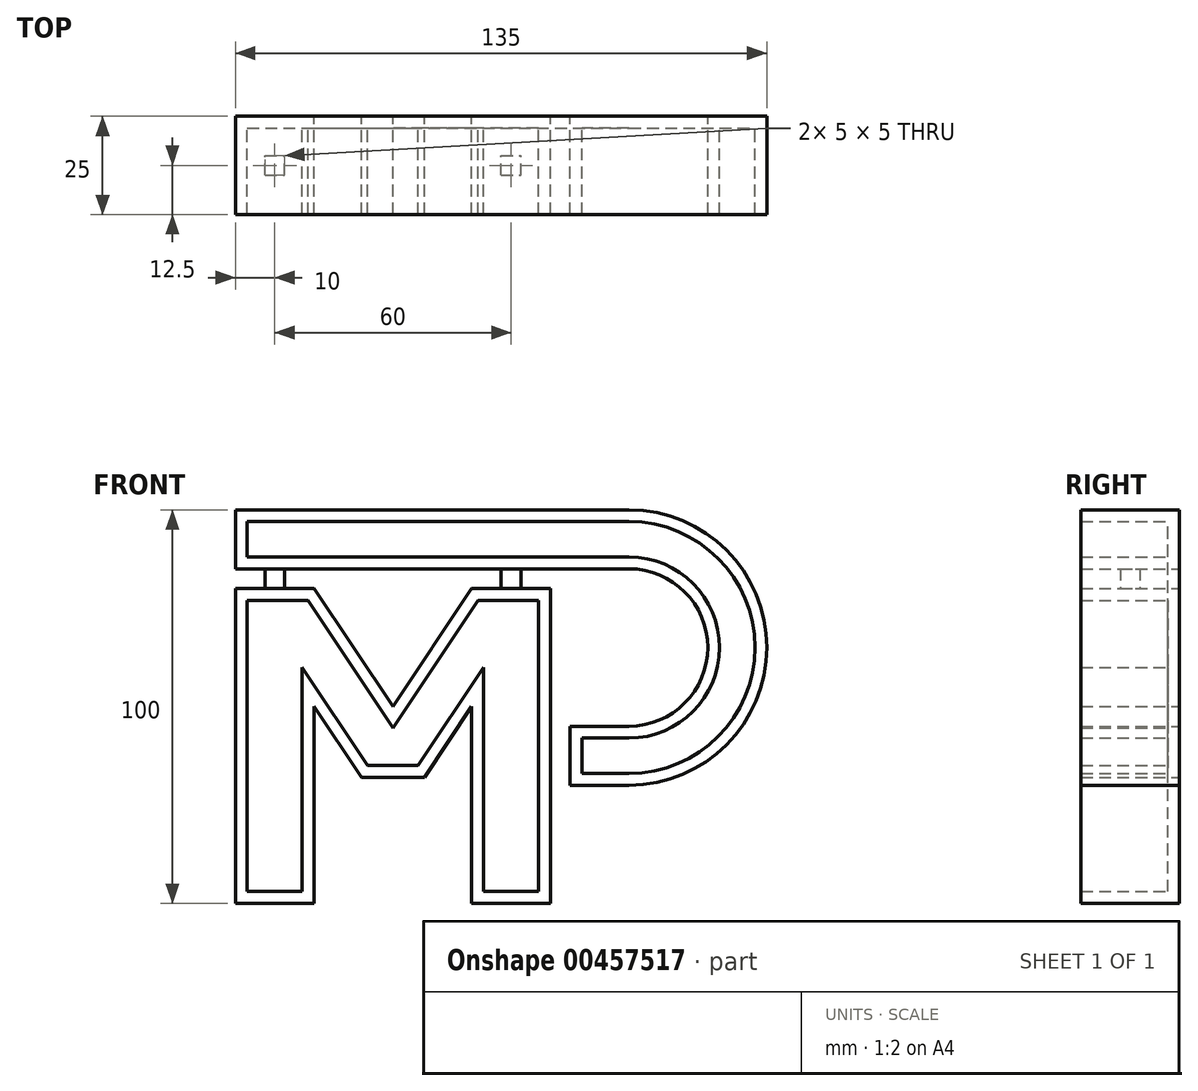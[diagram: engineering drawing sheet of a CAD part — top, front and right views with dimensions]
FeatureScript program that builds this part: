
annotation { "Feature Type Name" : "Feature", "Feature Type Description" : "" }
export const myFeature = defineFeature(function(context is Context, id is Id, definition is map)
    precondition{}
    {
        {
            var Q0;
            Q0=qCreatedBy(makeId("Top.planeOp"),FACE);
            cPlane(context, id + "F0", {"entities" : qUnion([Q0]), "cplaneType" : CPlaneType.OFFSET, "offset" : 80 * mm, "width" : 150 * mm, "height" : 150 * mm});
        }
        {
            var Q0;
            Q0=qCreatedBy(makeId("Front.planeOp"),FACE);
            var sketch = newSketch(context, id + "F1", { "sketchPlane" : qUnion([Q0])});
            skLineSegment(sketch, "E0", {"start": v(-40, 0) * mm, "end": v(-40, 80) * mm});
            skLineSegment(sketch, "E1", {"start": v(-40, 80) * mm, "end": v(-20, 80) * mm});
            skLineSegment(sketch, "E2", {"start": v(-20, 80) * mm, "end": v(0, 50) * mm});
            skLineSegment(sketch, "E3", {"start": v(-20, 0) * mm, "end": v(-20, 50) * mm});
            skLineSegment(sketch, "E4", {"start": v(0, 30) * mm, "end": v(0, 30) * mm});
            skLineSegment(sketch, "E5", {"start": v(-20, 50) * mm, "end": v(-8, 32) * mm});
            skLineSegment(sketch, "E6", {"start": v(-8, 32) * mm, "end": v(0, 32) * mm});
            skLineSegment(sketch, "E7.MirrorCS", {"start": v(20, 80) * mm, "end": v(0, 50) * mm});
            skLineSegment(sketch, "E8.MirrorCS", {"start": v(40, 80) * mm, "end": v(20, 80) * mm});
            skLineSegment(sketch, "E9.MirrorCS", {"start": v(40, 0) * mm, "end": v(40, 80) * mm});
            skLineSegment(sketch, "E10.MirrorCS", {"start": v(40, 0) * mm, "end": v(20, 0) * mm});
            skLineSegment(sketch, "E11.MirrorCS", {"start": v(20, 0) * mm, "end": v(20, 50) * mm});
            skLineSegment(sketch, "E12.MirrorCS", {"start": v(20, 50) * mm, "end": v(8, 32) * mm});
            skLineSegment(sketch, "E13.MirrorCS", {"start": v(8, 32) * mm, "end": v(0, 32) * mm});
            skLineSegment(sketch, "E14", {"start": v(-40, 0) * mm, "end": v(-20, 0) * mm});
            skSolve(sketch);
        }
        {
            var Q0;
            Q0=qCreatedBy(makeId("Front.planeOp"),FACE);
            var sketch = newSketch(context, id + "F2", { "sketchPlane" : qUnion([Q0])});
            skLineSegment(sketch, "E15", {"start": v(-40, 85) * mm, "end": v(60, 85) * mm});
            skLineSegment(sketch, "E16", {"start": v(-40, 85) * mm, "end": v(-40, 100) * mm});
            skLineSegment(sketch, "E17", {"start": v(-40, 100) * mm, "end": v(60, 100) * mm});
            skLineSegment(sketch, "E18", {"start": v(60, 45) * mm, "end": v(45, 45) * mm});
            skLineSegment(sketch, "E19", {"start": v(45, 45) * mm, "end": v(45, 30) * mm});
            skLineSegment(sketch, "E20", {"start": v(45, 30) * mm, "end": v(60, 30) * mm});
            skArc(sketch, "E21", {"start": v(60, 85) * mm, "mid": v(80, 65) * mm, "end": v(60, 45) * mm});
            skArc(sketch, "E22", {"start": v(60, 100) * mm, "mid": v(95, 65) * mm, "end": v(60, 30) * mm});
            skSolve(sketch);
        }
        {
            var Q0;
            Q0 = qSketchRegion(id + "F1", true);
            var Q1;
            Q1 = qSketchRegion(id + "F2", true);
            var Q2;
            Q2=makeQuery(id+"F2.imprint","IMPRINT",FACE,{"disambiguationData":[TD([[makeQuery(id+"F2.imprint","IMPRINT",EDGE,{"derivedFrom":sQuery(id+"F2.wireOp",EDGE,"E15")}),1.0]])]});
            var Q3;
            Q3=makeQuery(id+"F1.imprint","IMPRINT",FACE,{"disambiguationData":[TD([[makeQuery(id+"F1.imprint","IMPRINT",EDGE,{"derivedFrom":sQuery(id+"F1.wireOp",EDGE,"E0")}),-1.0]])]});
            extrude(context, id + "F3", {"entities" : qUnion([Q0, Q1, Q2, Q3]), "depth" : 25 * mm});
        }
        {
            var Q0;
            Q0=makeQuery(id+"F3.opExtrude","CAP_FACE",FACE,{"disambiguationData":[OSD([sQuery(id+"F1.wireOp",EDGE,"E0"),sQuery(id+"F1.wireOp",EDGE,"E1"),sQuery(id+"F1.wireOp",EDGE,"E2"),sQuery(id+"F1.wireOp",EDGE,"ab83c112-5276-4321-8634-02bc0d65a358"),sQuery(id+"F1.wireOp",EDGE,"E3"),sQuery(id+"F1.wireOp",EDGE,"E5"),sQuery(id+"F1.wireOp",EDGE,"E6"),sQuery(id+"F1.wireOp",EDGE,"E7.MirrorCS"),sQuery(id+"F1.wireOp",EDGE,"E8.MirrorCS"),sQuery(id+"F1.wireOp",EDGE,"E9.MirrorCS"),sQuery(id+"F1.wireOp",EDGE,"E10.MirrorCS"),sQuery(id+"F1.wireOp",EDGE,"E11.MirrorCS"),sQuery(id+"F1.wireOp",EDGE,"E12.MirrorCS"),sQuery(id+"F1.wireOp",EDGE,"E13.MirrorCS")])],"isStart":false});
            var Q1;
            Q1=makeQuery(id+"F3.opExtrude","CAP_FACE",FACE,{"disambiguationData":[OSD([sQuery(id+"F2.wireOp",EDGE,"E15"),sQuery(id+"F2.wireOp",EDGE,"E16"),sQuery(id+"F2.wireOp",EDGE,"E17"),sQuery(id+"F2.wireOp",EDGE,"E18"),sQuery(id+"F2.wireOp",EDGE,"E19"),sQuery(id+"F2.wireOp",EDGE,"E20"),sQuery(id+"F2.wireOp",EDGE,"E21"),sQuery(id+"F2.wireOp",EDGE,"E22")])],"isStart":false});
            shell(context, id + "F4", {"entities" : qUnion([Q0, Q1]), "thickness" : 3 * mm});
        }
        {
            var Q0;
            Q0=qCreatedBy(id+"F0.planeOp",FACE);
            var sketch = newSketch(context, id + "F5", { "sketchPlane" : qUnion([Q0])});
            skLineSegment(sketch, "E23.bottom", {"start": v(-32.5, -15) * mm, "end": v(-27.5, -15) * mm});
            skLineSegment(sketch, "E23.top", {"start": v(-32.5, -10) * mm, "end": v(-27.5, -10) * mm});
            skLineSegment(sketch, "E23.left", {"start": v(-32.5, -15) * mm, "end": v(-32.5, -10) * mm});
            skLineSegment(sketch, "E23.right", {"start": v(-27.5, -15) * mm, "end": v(-27.5, -10) * mm});
            skLineSegment(sketch, "E24.bottom", {"start": v(27.5, -15) * mm, "end": v(32.5, -15) * mm});
            skLineSegment(sketch, "E24.top", {"start": v(27.5, -10) * mm, "end": v(32.5, -10) * mm});
            skLineSegment(sketch, "E24.left", {"start": v(27.5, -15) * mm, "end": v(27.5, -10) * mm});
            skLineSegment(sketch, "E24.right", {"start": v(32.5, -15) * mm, "end": v(32.5, -10) * mm});
            skSolve(sketch);
        }
        {
            var Q0;
            Q0 = qSketchRegion(id + "F5", true);
            extrude(context, id + "F6", {"entities" : qUnion([Q0]), "operationType" : NewBodyOperationType.ADD, "depth" : 5 * mm});
        }
    });
